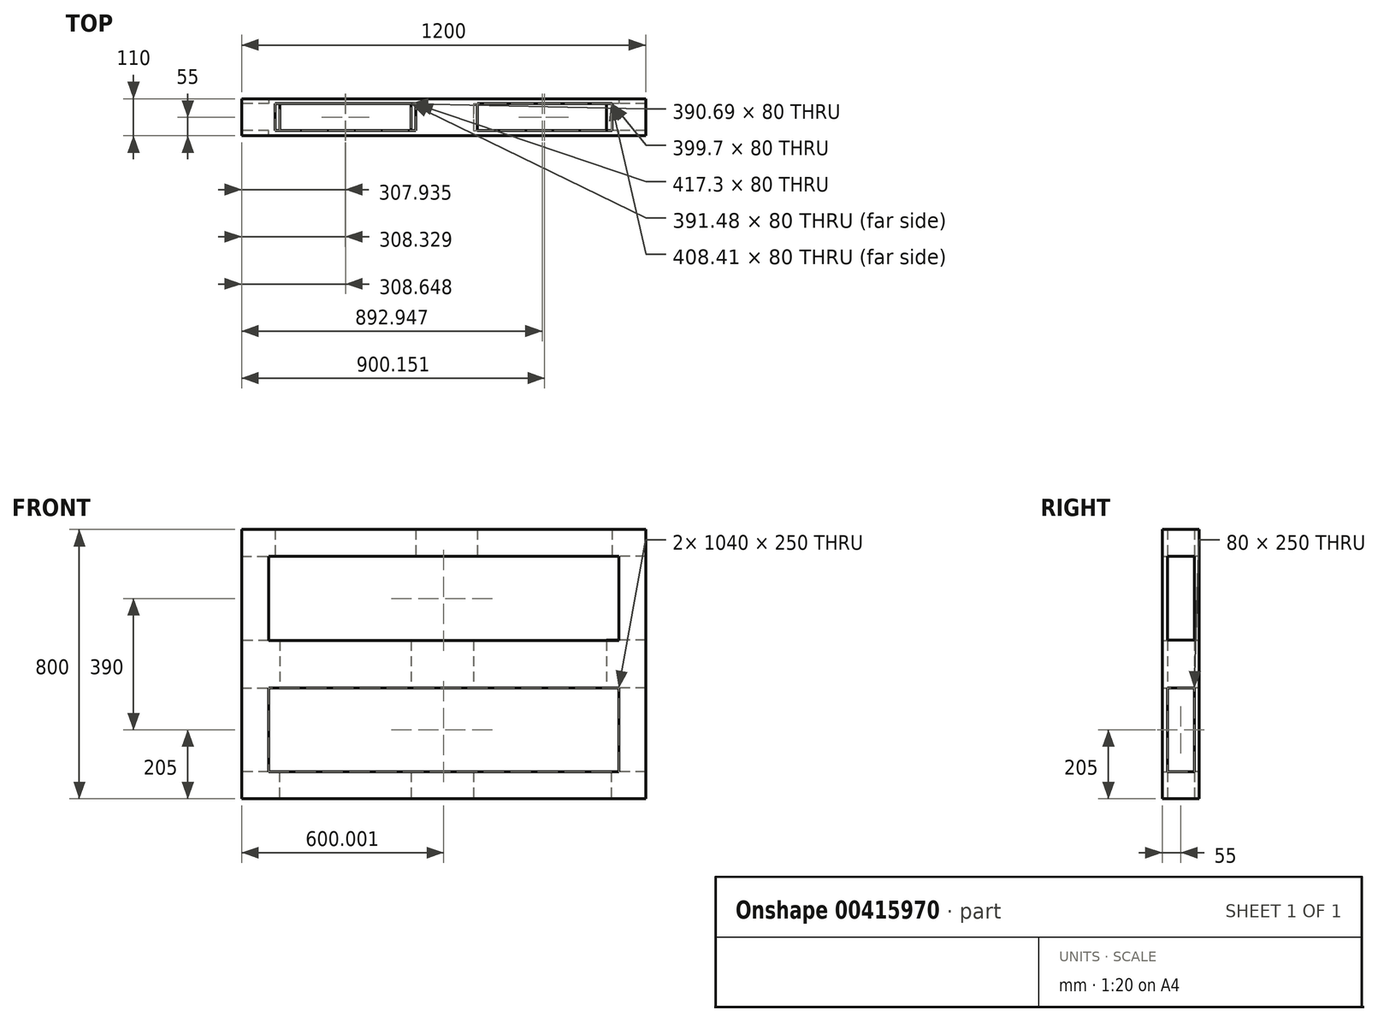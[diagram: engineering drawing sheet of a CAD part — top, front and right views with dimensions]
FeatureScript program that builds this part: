
annotation { "Feature Type Name" : "Feature", "Feature Type Description" : "" }
export const myFeature = defineFeature(function(context is Context, id is Id, definition is map)
    precondition{}
    {
        {
            var Q0;
            Q0=qCreatedBy(makeId("Front.planeOp"),FACE);
            var sketch = newSketch(context, id + "F0", { "sketchPlane" : qUnion([Q0])});
            skLineSegment(sketch, "E0.bottom", {"start": v(-616.76, 400) * mm, "end": v(583.24, 400) * mm});
            skLineSegment(sketch, "E0.top", {"start": v(-616.76, -400) * mm, "end": v(583.24, -400) * mm});
            skLineSegment(sketch, "E0.left", {"start": v(-616.76, 400) * mm, "end": v(-616.76, -400) * mm});
            skLineSegment(sketch, "E0.right", {"start": v(583.24, 400) * mm, "end": v(583.24, -400) * mm});
            skLineSegment(sketch, "E1.bottom", {"start": v(-536.76, 320) * mm, "end": v(503.24, 320) * mm});
            skLineSegment(sketch, "E1.top", {"start": v(-536.76, 70) * mm, "end": v(503.24, 70) * mm});
            skLineSegment(sketch, "E1.left", {"start": v(-536.76, 320) * mm, "end": v(-536.76, 70) * mm});
            skLineSegment(sketch, "E1.right", {"start": v(503.24, 320) * mm, "end": v(503.24, 70) * mm});
            skLineSegment(sketch, "E2.bottom", {"start": v(-536.76, -70) * mm, "end": v(503.24, -70) * mm});
            skLineSegment(sketch, "E2.top", {"start": v(-536.76, -320) * mm, "end": v(503.24, -320) * mm});
            skLineSegment(sketch, "E2.left", {"start": v(-536.76, -70) * mm, "end": v(-536.76, -320) * mm});
            skLineSegment(sketch, "E2.right", {"start": v(503.24, -70) * mm, "end": v(503.24, -320) * mm});
            skSolve(sketch);
        }
        {
            var Q0;
            Q0=makeQuery(id+"F0.imprint","IMPRINT",FACE,{"disambiguationData":[TD([[makeQuery(id+"F0.imprint","IMPRINT",EDGE,{"derivedFrom":sQuery(id+"F0.wireOp",EDGE,"E0.bottom")}),-1.0]])]});
            extrude(context, id + "F1", {"entities" : qUnion([Q0]), "depth" : 15 * mm});
        }
        {
            var Q0;
            Q0=makeQuery(id+"F1.opExtrude","CAP_FACE",FACE,{"disambiguationData":[OSD([sQuery(id+"F0.wireOp",EDGE,"E0.bottom"),sQuery(id+"F0.wireOp",EDGE,"E0.top"),sQuery(id+"F0.wireOp",EDGE,"E0.left"),sQuery(id+"F0.wireOp",EDGE,"E0.right"),sQuery(id+"F0.wireOp",EDGE,"E1.bottom"),sQuery(id+"F0.wireOp",EDGE,"E1.top"),sQuery(id+"F0.wireOp",EDGE,"E1.left"),sQuery(id+"F0.wireOp",EDGE,"E1.right"),sQuery(id+"F0.wireOp",EDGE,"E2.bottom"),sQuery(id+"F0.wireOp",EDGE,"E2.top"),sQuery(id+"F0.wireOp",EDGE,"E2.left"),sQuery(id+"F0.wireOp",EDGE,"E2.right")])],"isStart":true});
            var sketch = newSketch(context, id + "F2", { "sketchPlane" : qUnion([Q0])});
            skLineSegment(sketch, "E3.bottom", {"start": v(516.76, 400) * mm, "end": v(616.76, 400) * mm});
            skLineSegment(sketch, "E3.top", {"start": v(516.76, 320) * mm, "end": v(616.76, 320) * mm});
            skLineSegment(sketch, "E3.left", {"start": v(516.76, 400) * mm, "end": v(516.76, 320) * mm});
            skLineSegment(sketch, "E3.right", {"start": v(616.76, 400) * mm, "end": v(616.76, 320) * mm});
            skLineSegment(sketch, "E4.bottom", {"start": v(-583.24, 400) * mm, "end": v(-483.24, 400) * mm});
            skLineSegment(sketch, "E4.top", {"start": v(-583.24, 320) * mm, "end": v(-483.24, 320) * mm});
            skLineSegment(sketch, "E4.left", {"start": v(-583.24, 400) * mm, "end": v(-583.24, 320) * mm});
            skLineSegment(sketch, "E4.right", {"start": v(-483.24, 400) * mm, "end": v(-483.24, 320) * mm});
            skLineSegment(sketch, "E5.bottom", {"start": v(-583.24, 71.45) * mm, "end": v(-466.79, 71.45) * mm});
            skLineSegment(sketch, "E5.top", {"start": v(-583.24, -70) * mm, "end": v(-466.79, -70) * mm});
            skLineSegment(sketch, "E5.left", {"start": v(-583.24, 71.45) * mm, "end": v(-583.24, -70) * mm});
            skLineSegment(sketch, "E5.right", {"start": v(-466.79, 71.45) * mm, "end": v(-466.79, -70) * mm});
            skLineSegment(sketch, "E6.bottom", {"start": v(503.78, 70) * mm, "end": v(616.76, 70) * mm});
            skLineSegment(sketch, "E6.top", {"start": v(503.78, -70) * mm, "end": v(616.76, -70) * mm});
            skLineSegment(sketch, "E6.left", {"start": v(503.78, 70) * mm, "end": v(503.78, -70) * mm});
            skLineSegment(sketch, "E6.right", {"start": v(616.76, 70) * mm, "end": v(616.76, -70) * mm});
            skLineSegment(sketch, "E7.bottom", {"start": v(-71.98, 70) * mm, "end": v(113.08, 70) * mm});
            skLineSegment(sketch, "E7.top", {"start": v(-71.98, -70) * mm, "end": v(113.08, -70) * mm});
            skLineSegment(sketch, "E7.left", {"start": v(-71.98, 70) * mm, "end": v(-71.98, -70) * mm});
            skLineSegment(sketch, "E7.right", {"start": v(113.08, 70) * mm, "end": v(113.08, -70) * mm});
            skLineSegment(sketch, "E8.bottom", {"start": v(-583.24, -320) * mm, "end": v(-480.4, -320) * mm});
            skLineSegment(sketch, "E8.top", {"start": v(-583.24, -400) * mm, "end": v(-480.4, -400) * mm});
            skLineSegment(sketch, "E8.left", {"start": v(-583.24, -320) * mm, "end": v(-583.24, -400) * mm});
            skLineSegment(sketch, "E8.right", {"start": v(-480.4, -320) * mm, "end": v(-480.4, -400) * mm});
            skLineSegment(sketch, "E9.bottom", {"start": v(504.57, -320) * mm, "end": v(616.76, -320) * mm});
            skLineSegment(sketch, "E9.top", {"start": v(504.57, -400) * mm, "end": v(616.76, -400) * mm});
            skLineSegment(sketch, "E9.left", {"start": v(504.57, -320) * mm, "end": v(504.57, -400) * mm});
            skLineSegment(sketch, "E9.right", {"start": v(616.76, -320) * mm, "end": v(616.76, -400) * mm});
            skLineSegment(sketch, "E10.bottom", {"start": v(-83.54, 400) * mm, "end": v(99.46, 400) * mm});
            skLineSegment(sketch, "E10.top", {"start": v(-83.54, 320) * mm, "end": v(99.46, 320) * mm});
            skLineSegment(sketch, "E10.left", {"start": v(-83.54, 400) * mm, "end": v(-83.54, 320) * mm});
            skLineSegment(sketch, "E10.right", {"start": v(99.46, 400) * mm, "end": v(99.46, 320) * mm});
            skPoint(sketch, "E11.oppositeSnap0", {"position": v(113.08, 0) * mm});
            skLineSegment(sketch, "E11.bottom", {"start": v(-71.98, -320) * mm, "end": v(113.08, -320) * mm});
            skLineSegment(sketch, "E11.top", {"start": v(-71.98, -400) * mm, "end": v(113.08, -400) * mm});
            skLineSegment(sketch, "E11.left", {"start": v(-71.98, -320) * mm, "end": v(-71.98, -400) * mm});
            skLineSegment(sketch, "E11.right", {"start": v(113.08, -320) * mm, "end": v(113.08, -400) * mm});
            skSolve(sketch);
        }
        {
            var Q0;
            Q0=makeQuery(id+"F2.imprint","IMPRINT",FACE,{"disambiguationData":[TD([[makeQuery(id+"F2.imprint","IMPRINT",EDGE,{"derivedFrom":sQuery(id+"F2.wireOp",EDGE,"E7.bottom")}),1.0]])]});
            var Q1;
            {var subQ4=sQuery(id+"F2.wireOp",EDGE,"E6.left");Q1=makeQuery(id+"F2.imprint","IMPRINT",FACE,{"disambiguationData":[TD([[makeQuery(id+"F2.imprint","IMPRINT",EDGE,{"derivedFrom":subQ4}),1.0]])]});}
            var Q2;
            Q2=makeQuery(id+"F2.imprint","IMPRINT",FACE,{"disambiguationData":[TD([[makeQuery(id+"F2.imprint","IMPRINT",EDGE,{"derivedFrom":sQuery(id+"F2.wireOp",EDGE,"E9.top")}),-1.0]])]});
            var Q3;
            Q3=makeQuery(id+"F2.imprint","IMPRINT",FACE,{"disambiguationData":[TD([[makeQuery(id+"F2.imprint","IMPRINT",EDGE,{"derivedFrom":sQuery(id+"F2.wireOp",EDGE,"E8.top")}),-1.0]])]});
            var Q4;
            {var subQ0=sQuery(id+"F2.wireOp",EDGE,"E5.left");Q4=makeQuery(id+"F2.imprint","IMPRINT",FACE,{"disambiguationData":[TD([[makeQuery(id+"F2.imprint","IMPRINT",EDGE,{"derivedFrom":subQ0}),1.0]])]});}
            var Q5;
            Q5=makeQuery(id+"F2.imprint","IMPRINT",FACE,{"disambiguationData":[TD([[makeQuery(id+"F2.imprint","IMPRINT",EDGE,{"derivedFrom":sQuery(id+"F2.wireOp",EDGE,"E4.bottom")}),1.0]])]});
            var Q6;
            Q6=makeQuery(id+"F2.imprint","IMPRINT",FACE,{"disambiguationData":[TD([[makeQuery(id+"F2.imprint","IMPRINT",EDGE,{"derivedFrom":sQuery(id+"F2.wireOp",EDGE,"E3.bottom")}),1.0]])]});
            extrude(context, id + "F3", {"entities" : qUnion([Q0, Q1, Q2, Q3, Q4, Q5, Q6]), "operationType" : NewBodyOperationType.ADD, "depth" : 40 * mm});
        }
        {
            var Q0;
            Q0 = qSketchRegion(id + "F2", true);
            extrude(context, id + "F4", {"entities" : qUnion([Q0]), "operationType" : NewBodyOperationType.ADD, "depth" : 40 * mm});
        }
        {
            var Q0;
            Q0=makeQuery(id+"F1.opExtrude","SWEPT_BODY",BODY,{"disambiguationData":[OSD([sQuery(id+"F0.wireOp",EDGE,"E0.bottom"),sQuery(id+"F0.wireOp",EDGE,"E0.top"),sQuery(id+"F0.wireOp",EDGE,"E0.left"),sQuery(id+"F0.wireOp",EDGE,"E0.right"),sQuery(id+"F0.wireOp",EDGE,"E1.bottom"),sQuery(id+"F0.wireOp",EDGE,"E1.top"),sQuery(id+"F0.wireOp",EDGE,"E1.left"),sQuery(id+"F0.wireOp",EDGE,"E1.right"),sQuery(id+"F0.wireOp",EDGE,"E2.bottom"),sQuery(id+"F0.wireOp",EDGE,"E2.top"),sQuery(id+"F0.wireOp",EDGE,"E2.left"),sQuery(id+"F0.wireOp",EDGE,"E2.right")])]});
            var Q1;
            Q1=makeQuery(id+"F3.opExtrude","CAP_FACE",FACE,{"disambiguationData":[OSD([sQuery(id+"F2.wireOp",EDGE,"E7.bottom"),sQuery(id+"F2.wireOp",EDGE,"E7.top"),sQuery(id+"F2.wireOp",EDGE,"E7.left"),sQuery(id+"F2.wireOp",EDGE,"E7.right")])],"isStart":false});
            mirror(context, id + "F5", {"operationType" : NewBodyOperationType.ADD, "entities" : qUnion([Q0]), "mirrorPlane" : qUnion([Q1])});
        }
    });
